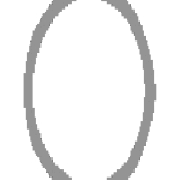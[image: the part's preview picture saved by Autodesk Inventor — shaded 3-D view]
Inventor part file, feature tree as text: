
AUTODESK INVENTOR PART (.ipt)
format: ipt  version: 2021 (Build 250183000, 183)  size: 112,640 bytes
history: native  units: in
note: dims shown in document units (in); Inventor stores cm internally (conversion verified against a paired STEP export)
features: other x4, sketch x3, plane x1
ambient origin geometry x8: Origin, YZ Plane, XZ Plane, XY Plane, X Axis, Y Axis, Z Axis, Center Point
bodies: Solid1 (feature_tree), Body (feature_tree)
feature tree (8):
  other  "Driven Length"
  other  "Frame Generator"
  other  "Start Plane"
  other  "End Plane"
  sketch  "Sketch"  dims[d2=14.3527in d4=-0.0in d5=14.3527in d6=0.12in d7=0.0in d8=90.0deg d9=14.3527in]
  sketch  "Sketch2"  dims[d0=1.0in]
  plane  "Work Plane3"
  sketch  "Sketch3"  dims[d1=0.065in]
